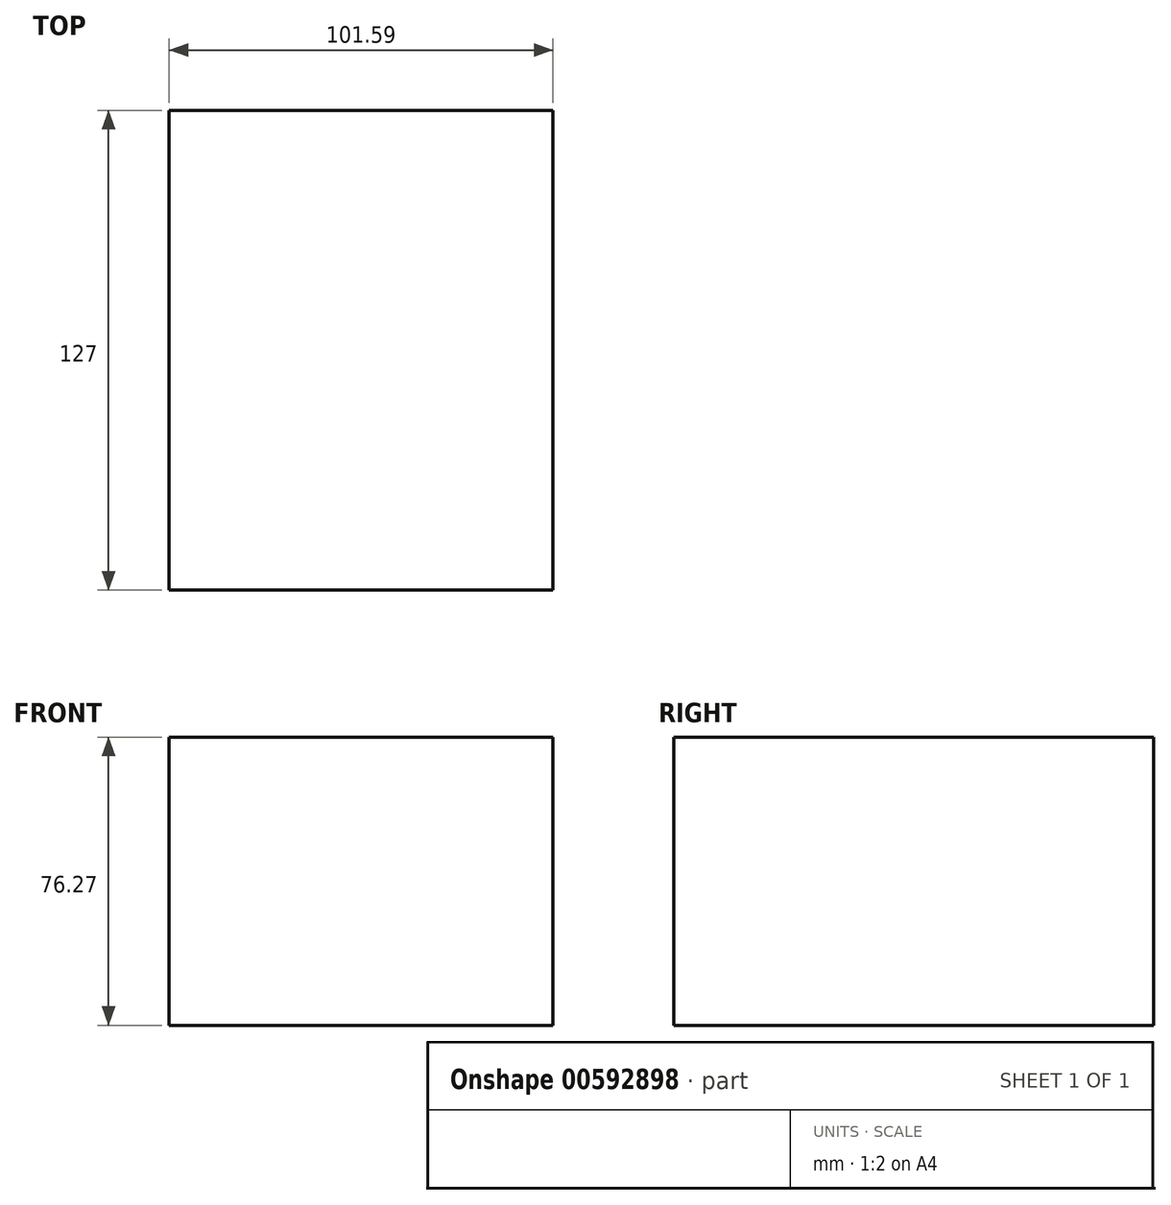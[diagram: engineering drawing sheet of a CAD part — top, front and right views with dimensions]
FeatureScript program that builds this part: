
annotation { "Feature Type Name" : "Feature", "Feature Type Description" : "" }
export const myFeature = defineFeature(function(context is Context, id is Id, definition is map)
    precondition{}
    {
        {
            var Q0;
            Q0=qCreatedBy(makeId("Front.planeOp"),FACE);
            var sketch = newSketch(context, id + "F0", { "sketchPlane" : qUnion([Q0])});
            skLineSegment(sketch, "E0.bottom", {"start": v(-72.67, 52.81) * mm, "end": v(28.92, 52.81) * mm});
            skLineSegment(sketch, "E0.top", {"start": v(-72.67, -23.46) * mm, "end": v(28.92, -23.46) * mm});
            skLineSegment(sketch, "E0.left", {"start": v(-72.67, 52.81) * mm, "end": v(-72.67, -23.46) * mm});
            skLineSegment(sketch, "E0.right", {"start": v(28.92, 52.81) * mm, "end": v(28.92, -23.46) * mm});
            skSolve(sketch);
        }
        {
            var Q0;
            Q0 = qSketchRegion(id + "F0", true);
            extrude(context, id + "F1", {"entities" : qUnion([Q0]), "depth" : 127 * mm, "offsetDistance" : 25.4 * mm});
        }
    });
